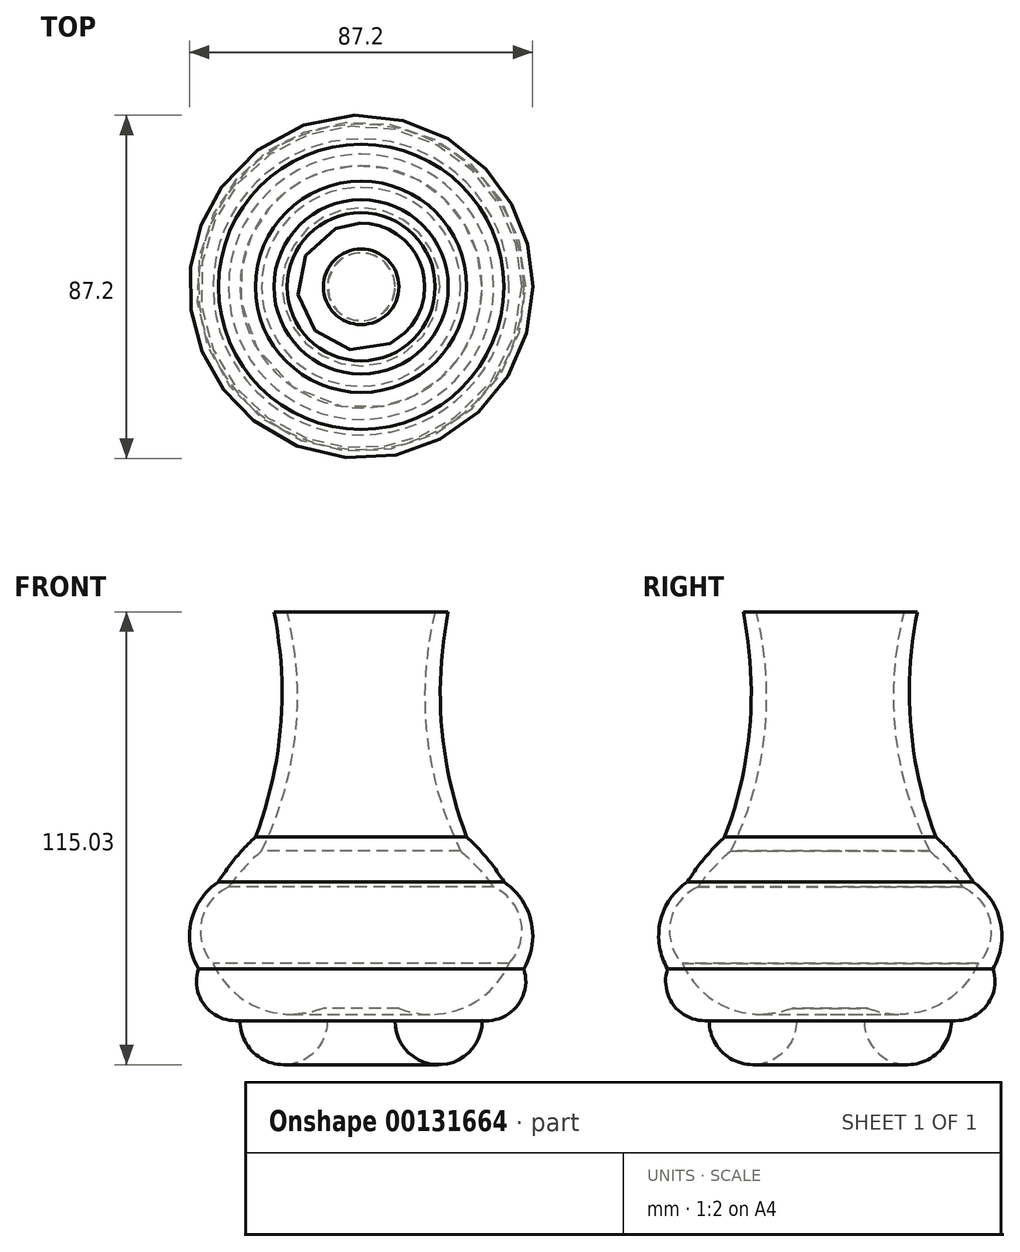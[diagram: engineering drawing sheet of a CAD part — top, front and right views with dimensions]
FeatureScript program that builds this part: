
annotation { "Feature Type Name" : "Feature", "Feature Type Description" : "" }
export const myFeature = defineFeature(function(context is Context, id is Id, definition is map)
    precondition{}
    {
        {
            var Q0;
            Q0=qCreatedBy(makeId("Front.planeOp"),FACE);
            var sketch = newSketch(context, id + "F0", { "sketchPlane" : qUnion([Q0])});
            skLineSegment(sketch, "E0", {"start": v(0, -48.67) * mm, "end": v(8.62, -48.67) * mm});
            skArc(sketch, "E1", {"start": v(8.62, -48.67) * mm, "mid": v(19.68, -59.89) * mm, "end": v(30.75, -48.67) * mm});
            skArc(sketch, "E2", {"start": v(30.75, -48.67) * mm, "mid": v(39.62, -45) * mm, "end": v(41.33, -35.55) * mm});
            skArc(sketch, "E3", {"start": v(41.33, -35.55) * mm, "mid": v(43.18, -23.47) * mm, "end": v(36.23, -13.42) * mm});
            skArc(sketch, "E4", {"start": v(36.23, -13.42) * mm, "mid": v(31.94, -7.4) * mm, "end": v(26.83, -2.06) * mm});
            skArc(sketch, "E5", {"start": v(22.13, 55.14) * mm, "mid": v(20.45, 26.2) * mm, "end": v(26.83, -2.06) * mm});
            skLineSegment(sketch, "E6", {"start": v(22.13, 55.14) * mm, "end": v(18.8, 55.14) * mm});
            skArc(sketch, "E7", {"start": v(18.8, 55.14) * mm, "mid": v(16.66, 24.2) * mm, "end": v(25.27, -5.58) * mm});
            skArc(sketch, "E8", {"start": v(33.69, -14.79) * mm, "mid": v(29.74, -9.94) * mm, "end": v(25.27, -5.58) * mm});
            skArc(sketch, "E9", {"start": v(37.6, -34.18) * mm, "mid": v(40.6, -23.48) * mm, "end": v(33.69, -14.79) * mm});
            skArc(sketch, "E10", {"start": v(9.6, -45.54) * mm, "mid": v(25.9, -45.5) * mm, "end": v(37.6, -34.18) * mm});
            skLineSegment(sketch, "E11", {"start": v(9.6, -45.54) * mm, "end": v(0, -45.54) * mm});
            skLineSegment(sketch, "E12", {"start": v(0, -45.54) * mm, "end": v(0, -48.67) * mm});
            skSolve(sketch);
        }
        {
            var Q0;
            Q0=makeQuery(id+"F0.imprint","IMPRINT",FACE,{"disambiguationData":[TD([[makeQuery(id+"F0.imprint","IMPRINT",EDGE,{"derivedFrom":sQuery(id+"F0.wireOp",EDGE,"E0")}),1.0]])]});
            var Q1;
            Q1=sQuery(id+"F0.wireOp",EDGE,"E12");
            revolve(context, id + "F1", {"entities" : qUnion([Q0]), "axis" : qUnion([Q1]), "revolveType" : RevolveType.FULL});
        }
    });
